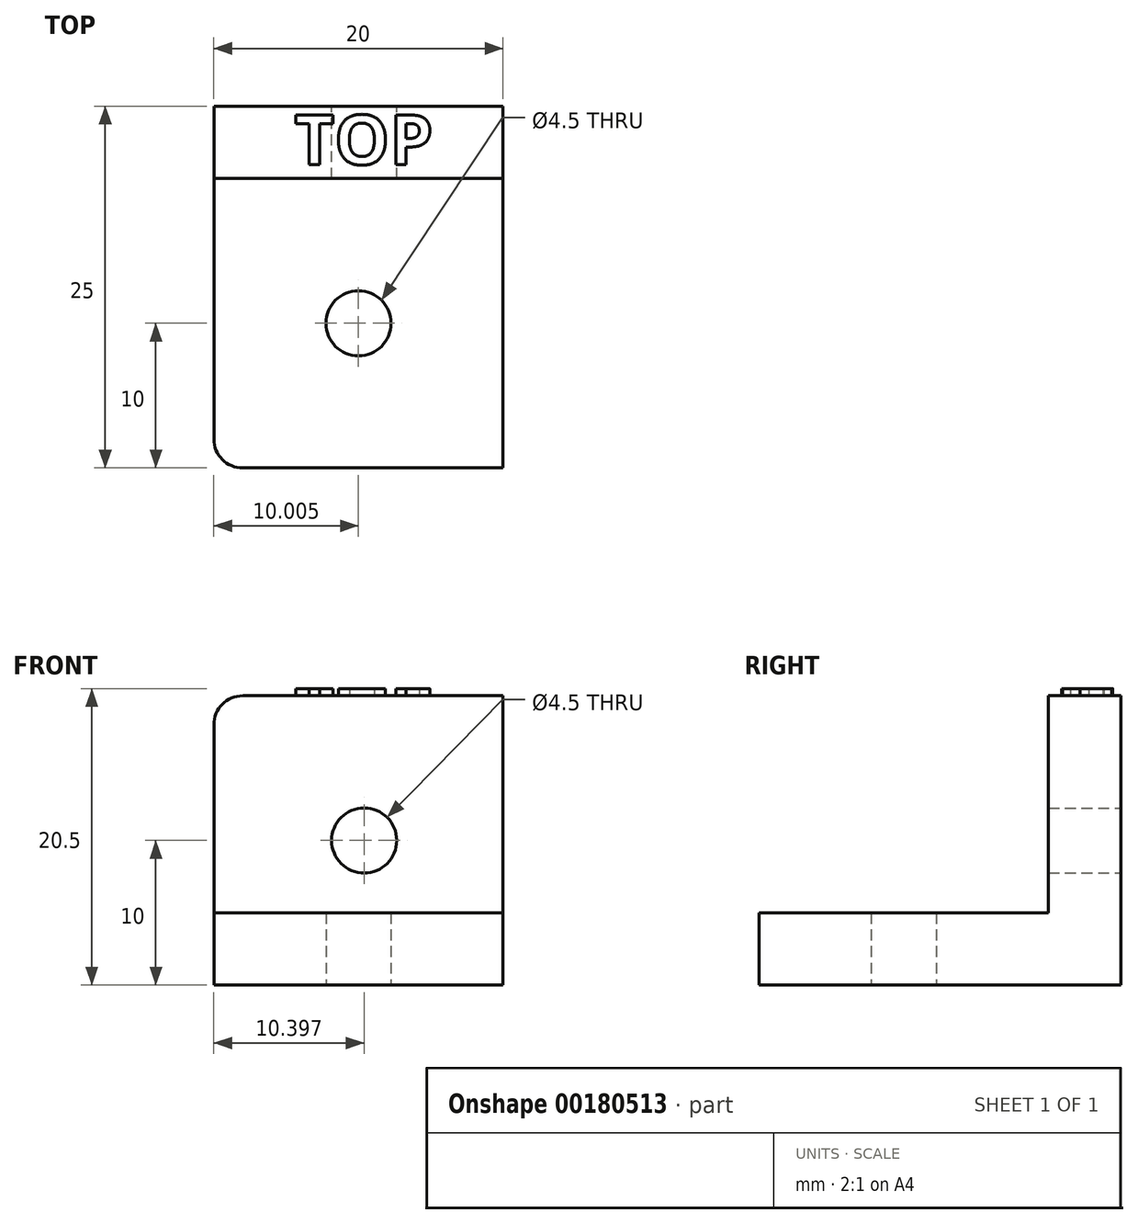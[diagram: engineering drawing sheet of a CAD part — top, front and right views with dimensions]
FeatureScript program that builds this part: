
annotation { "Feature Type Name" : "Feature", "Feature Type Description" : "" }
export const myFeature = defineFeature(function(context is Context, id is Id, definition is map)
    precondition{}
    {
        {
            var Q0;
            Q0=qCreatedBy(makeId("Top.planeOp"),FACE);
            var sketch = newSketch(context, id + "F0", { "sketchPlane" : qUnion([Q0])});
            skLineSegment(sketch, "E0.bottom", {"start": v(-9.66, 0) * mm, "end": v(10.34, 0) * mm});
            skLineSegment(sketch, "E0.top", {"start": v(-9.66, 25) * mm, "end": v(10.34, 25) * mm});
            skLineSegment(sketch, "E0.left", {"start": v(-9.66, 0) * mm, "end": v(-9.66, 25) * mm});
            skLineSegment(sketch, "E0.right", {"start": v(10.34, 0) * mm, "end": v(10.34, 25) * mm});
            skCircle(sketch, "E1", {"center": v(0.34, 10) * mm, "radius": 2.25 * mm});
            skPoint(sketch, "E2", {"position": v(0.34, 25) * mm});
            skPoint(sketch, "E3", {"position": v(-9.66, 10) * mm});
            skLineSegment(sketch, "E4", {"start": v(-9.66, 20) * mm, "end": v(10.34, 20) * mm});
            skSolve(sketch);
        }
        {
            var Q0;
            {var subQ1=sQuery(id+"F0.wireOp",EDGE,"E0.bottom");Q0=makeQuery(id+"F0.imprint","IMPRINT",FACE,{"disambiguationData":[TD([[makeQuery(id+"F0.imprint","IMPRINT",EDGE,{"derivedFrom":subQ1}),1.0]])]});}
            extrude(context, id + "F1", {"entities" : qUnion([Q0]), "depth" : 5 * mm});
        }
        {
            var Q0;
            {var subQ0=sQuery(id+"F0.wireOp",EDGE,"E0.top");Q0=makeQuery(id+"F0.imprint","IMPRINT",FACE,{"disambiguationData":[TD([[makeQuery(id+"F0.imprint","IMPRINT",EDGE,{"derivedFrom":subQ0}),-1.0]])]});}
            extrude(context, id + "F2", {"entities" : qUnion([Q0]), "operationType" : NewBodyOperationType.ADD, "depth" : 20 * mm});
        }
        {
            var Q0;
            Q0=makeQuery(id+"F2.opExtrude","CAP_EDGE",EDGE,{"disambiguationData":[OSD([sQuery(id+"F0.wireOp",EDGE,"E0.left")])],"isStart":false});
            var Q1;
            Q1=makeQuery(id+"F1.opExtrude","SWEPT_EDGE",EDGE,{"disambiguationData":[OSD([sQuery(id+"F0.wireOp",EDGE,"E0.bottom"),sQuery(id+"F0.wireOp",EDGE,"E0.left")])]});
            var Q2;
            Q2=makeQuery(id+"F1.opExtrude","CAP_EDGE",EDGE,{"disambiguationData":[OSD([sQuery(id+"F0.wireOp",EDGE,"E4")])],"isStart":false});
            fillet(context, id + "F3", {"entities" : qUnion([Q0, Q1, Q2]), "radius" : 2 * mm, "tangentPropagation" : true, "allowEdgeOverflow" : false});
        }
        {
            var Q0;
            Q0=makeQuery(id+"F2.opExtrude","SWEPT_FACE",FACE,{"disambiguationData":[OSD([sQuery(id+"F0.wireOp",EDGE,"E0.top")])]});
            var sketch = newSketch(context, id + "F4", { "sketchPlane" : qUnion([Q0])});
            skCircle(sketch, "E5", {"center": v(-0.74, 10) * mm, "radius": 2.25 * mm});
            skSolve(sketch);
        }
        {
            var Q0;
            Q0=qSketchRegion(id+"F4",true);
            extrude(context, id + "F5", {"entities" : qUnion([Q0]), "operationType" : NewBodyOperationType.REMOVE, "oppositeDirection" : true, "depth" : 6 * mm});
        }
        {
            var Q0;
            Q0=makeQuery(id+"F2.opExtrude","CAP_FACE",FACE,{"disambiguationData":[OSD([sQuery(id+"F0.wireOp",EDGE,"E0.top"),sQuery(id+"F0.wireOp",EDGE,"E0.left"),sQuery(id+"F0.wireOp",EDGE,"E0.right"),sQuery(id+"F0.wireOp",EDGE,"E4")])],"isStart":false});
            var sketch = newSketch(context, id + "F6", { "sketchPlane" : qUnion([Q0])});
            skText(sketch, "E6", { "text": "TOP", "fontName": "OpenSans-Bold.ttf"});
            const initialGuessF6  = {"E6": [-0.0041, 0.02097, 1, 0, 0.00345]};
            skSetInitialGuess(sketch, initialGuessF6);
            skSolve(sketch);
        }
        {
            var Q0;
            Q0=qSketchRegion(id+"F6",true);
            extrude(context, id + "F7", {"entities" : qUnion([Q0]), "operationType" : NewBodyOperationType.ADD, "depth" : 0.5 * mm});
        }
    });
